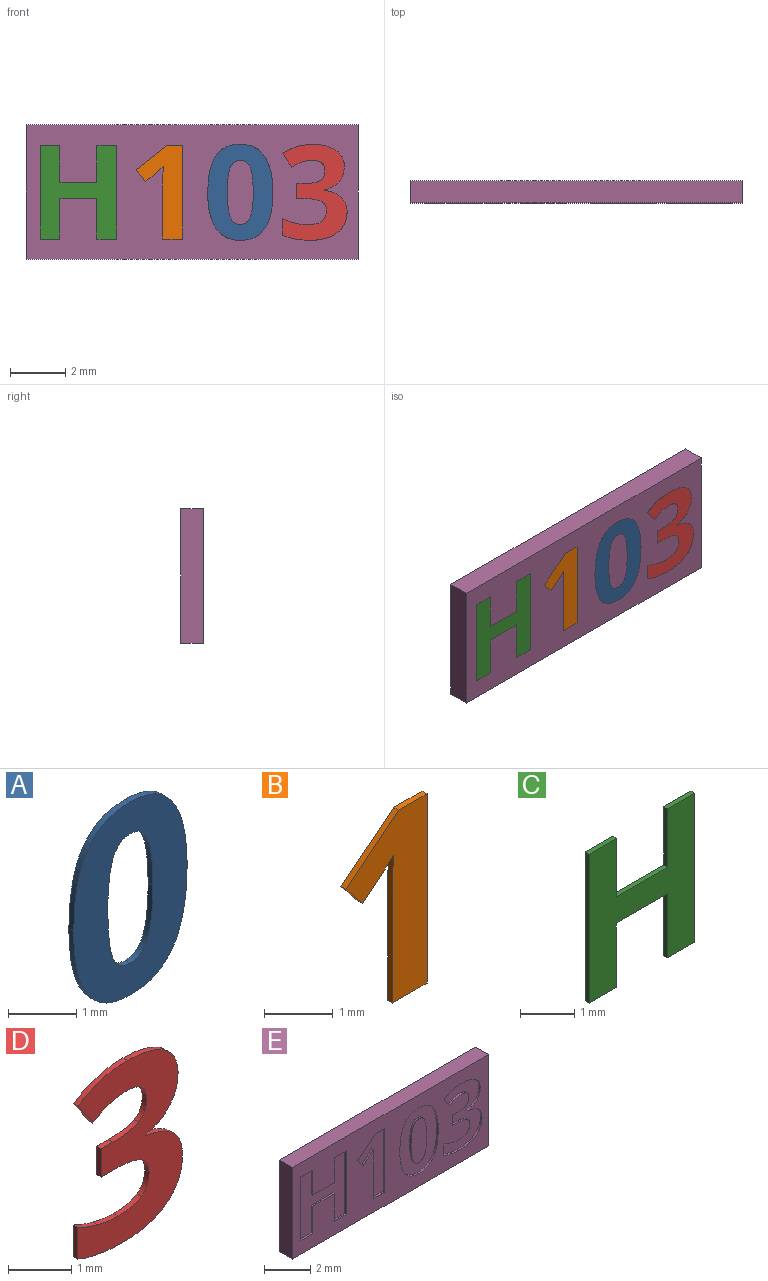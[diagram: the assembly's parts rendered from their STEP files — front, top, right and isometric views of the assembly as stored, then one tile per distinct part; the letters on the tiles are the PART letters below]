
ASSEMBLY  parts=5 mates=4
PART A: 18 faces, bbox 2.4x0.1x3.5 mm
  f0: plane 3.47x2.36mm, normal (0,-1,0), area 5mm2, adj f1,f2,f3,f4,f5,f6,f7,f8
  f1: extruded ~0.88x0.44mm, area 0.1mm2, adj f0,f2,f11,f13
  f2: extruded ~0.89x0.42mm, area 0.1mm2, adj f0,f1,f3,f11
  f3: extruded ~1.32x0.29mm, area 0.1mm2, adj f0,f2,f4,f11
  f4: extruded ~1.29x0.3mm, area 0.1mm2, adj f0,f3,f5,f11
  f5: extruded ~0.88x0.44mm, area 0.1mm2, adj f0,f4,f11,f12
  f6: extruded ~0.36x0.27mm, area 0mm2, adj f0,f7,f11,f16
  f7: extruded ~0.36x0.27mm, area 0mm2, adj f0,f6,f8,f11
  f8: extruded ~0.89x0.11mm, area 0.1mm2, adj f0,f7,f9,f11
  f9: extruded ~0.89x0.11mm, area 0.1mm2, adj f0,f8,f10,f11
  f10: extruded ~0.36x0.27mm, area 0mm2, adj f0,f9,f11,f15
  f11: plane 3.47x2.36mm, normal (0,1,0), area 5mm2, adj f1,f2,f3,f4,f5,f6,f7,f8
  f12: extruded ~0.89x0.42mm, area 0.1mm2, adj f0,f5,f11,f14
  f13: extruded ~1.3x0.3mm, area 0.1mm2, adj f0,f1,f11,f14
  f14: extruded ~1.31x0.29mm, area 0.1mm2, adj f0,f11,f12,f13
  f15: extruded ~0.36x0.27mm, area 0mm2, adj f0,f10,f11,f17
  f16: extruded ~0.89x0.11mm, area 0.1mm2, adj f0,f6,f11,f17
  f17: extruded ~0.89x0.11mm, area 0.1mm2, adj f0,f11,f15,f16
PART B: 12 faces, bbox 1.7x0.1x3.4 mm
  f0: plane 3.37x1.67mm, normal (0,-1,0), area 2.9mm2, adj f1,f2,f3,f4,f5,f6,f7,f9
  f1: plane 0.59x0.1mm, normal (0,0,1), area 0.1mm2, adj f0,f2,f8,f10
  f2: plane 1.09x0.86mm, normal (-0.62,0,0.78), area 0.1mm2, adj f0,f1,f3,f8
  f3: plane 0.43x0.34mm, normal (-0.78,0,-0.63), area 0.1mm2, adj f0,f2,f4,f8
  f4: plane 0.39x0.31mm, normal (0.63,0,-0.78), area 0mm2, adj f0,f3,f5,f8
  f5: extruded ~0.25x0.23mm, area 0mm2, adj f0,f4,f6,f8
  f6: plane 0.35x0.1mm, normal (-1,0,0.03), area 0mm2, adj f0,f5,f7,f8
  f7: plane 0.32x0.1mm, normal (-1,0,0.02), area 0mm2, adj f0,f6,f8,f9
  f8: plane 3.37x1.67mm, normal (0,1,0), area 2.9mm2, adj f1,f2,f3,f4,f5,f6,f7,f9
  f9: plane 1.95x0.1mm, normal (-1,0,0), area 0.2mm2, adj f0,f7,f8,f11
  f10: plane 3.37x0.1mm, normal (1,0,0), area 0.3mm2, adj f0,f1,f8,f11
  f11: plane 0.71x0.1mm, normal (0,0,-1), area 0.1mm2, adj f0,f8,f9,f10
PART C: 14 faces, bbox 2.8x0.1x3.4 mm
  f0: plane 3.37x2.76mm, normal (0,-1,0), area 5.6mm2, adj f1,f2,f3,f4,f5,f6,f7,f8
  f1: plane 0.71x0.1mm, normal (0,0,1), area 0.1mm2, adj f0,f2,f10,f12
  f2: plane 1.32x0.1mm, normal (-1,0,0), area 0.1mm2, adj f0,f1,f3,f10
  f3: plane 1.33x0.1mm, normal (0,0,1), area 0.1mm2, adj f0,f2,f4,f10
  f4: plane 1.32x0.1mm, normal (1,0,0), area 0.1mm2, adj f0,f3,f5,f10
  f5: plane 0.72x0.1mm, normal (0,0,1), area 0.1mm2, adj f0,f4,f6,f10
  f6: plane 3.37x0.1mm, normal (-1,0,0), area 0.3mm2, adj f0,f5,f7,f10
  f7: plane 0.72x0.1mm, normal (0,0,-1), area 0.1mm2, adj f0,f6,f8,f10
  f8: plane 1.46x0.1mm, normal (1,0,0), area 0.1mm2, adj f0,f7,f9,f10
  f9: plane 1.33x0.1mm, normal (0,0,-1), area 0.1mm2, adj f0,f8,f10,f11
  f10: plane 3.37x2.76mm, normal (0,1,0), area 5.6mm2, adj f1,f2,f3,f4,f5,f6,f7,f8
  f11: plane 1.46x0.1mm, normal (-1,0,0), area 0.1mm2, adj f0,f9,f10,f13
  f12: plane 3.37x0.1mm, normal (1,0,0), area 0.3mm2, adj f0,f1,f10,f13
  f13: plane 0.71x0.1mm, normal (0,0,-1), area 0.1mm2, adj f0,f10,f11,f12
PART D: 29 faces, bbox 2.3x0.1x3.5 mm
  f0: plane 3.47x2.33mm, normal (0,-1,0), area 4.3mm2, adj f1,f2,f3,f4,f5,f6,f7,f8
  f1: extruded ~0.83x0.21mm, area 0.1mm2, adj f0,f2,f25,f27
  f2: extruded ~1.1x0.33mm, area 0.1mm2, adj f0,f1,f3,f25
  f3: plane 0.49x0.33mm, normal (-0.83,0,-0.56), area 0.1mm2, adj f0,f2,f4,f25
  f4: extruded ~0.38x0.19mm, area 0mm2, adj f0,f3,f5,f25
  f5: extruded ~0.34x0.1mm, area 0mm2, adj f0,f4,f6,f25
  f6: extruded ~0.48x0.38mm, area 0.1mm2, adj f0,f5,f7,f25
  f7: extruded ~0.35x0.18mm, area 0mm2, adj f0,f6,f8,f25
  f8: extruded ~0.57x0.1mm, area 0.1mm2, adj f0,f7,f9,f25
  f9: plane 0.26x0.1mm, normal (0,0,1), area 0mm2, adj f0,f8,f10,f25
  f10: plane 0.55x0.1mm, normal (-1,0,0), area 0.1mm2, adj f0,f9,f11,f25
  f11: plane 0.26x0.1mm, normal (0,0,-1), area 0mm2, adj f0,f10,f12,f25
  f12: extruded ~0.62x0.1mm, area 0.1mm2, adj f0,f11,f13,f25
  f13: extruded ~0.34x0.19mm, area 0mm2, adj f0,f12,f14,f25
  f14: extruded ~0.39x0.17mm, area 0mm2, adj f0,f13,f15,f25
  f15: extruded ~0.52x0.12mm, area 0.1mm2, adj f0,f14,f16,f25
  f16: extruded ~0.47x0.1mm, area 0mm2, adj f0,f15,f17,f25
  f17: extruded ~0.43x0.16mm, area 0mm2, adj f0,f16,f18,f25
  f18: plane 0.61x0.1mm, normal (-1,0,0), area 0.1mm2, adj f0,f17,f19,f25
  f19: extruded ~0.97x0.18mm, area 0.1mm2, adj f0,f18,f20,f25
  f20: extruded ~1.01x0.27mm, area 0.1mm2, adj f0,f19,f21,f25
  f21: extruded ~0.76x0.35mm, area 0.1mm2, adj f0,f20,f22,f25
  f22: extruded ~0.53x0.21mm, area 0.1mm2, adj f0,f21,f23,f25
  f23: extruded ~0.62x0.25mm, area 0.1mm2, adj f0,f22,f24,f25
  f24: plane 0.1x0.01mm, normal (1,0,0), area 0mm2, adj f0,f23,f25,f26
  f25: plane 3.47x2.33mm, normal (0,1,0), area 4.3mm2, adj f1,f2,f3,f4,f5,f6,f7,f8
  f26: extruded ~0.54x0.3mm, area 0.1mm2, adj f0,f24,f25,f28
  f27: extruded ~0.59x0.3mm, area 0.1mm2, adj f0,f1,f25,f28
  f28: extruded ~0.54x0.19mm, area 0.1mm2, adj f0,f25,f26,f27
PART E: 76 faces, bbox 12x0.8x4.9 mm
  f0: plane 12x4.85mm, normal (0,-1,0), area 38.5mm2, adj f1,f2,f3,f4,f6,f7,f8,f9
  f1: plane 4.85x0.8mm, normal (1,0,0), area 3.9mm2, adj f0,f2,f4,f5
  f2: plane 12x0.8mm, normal (0,0,1), area 9.6mm2, adj f0,f1,f3,f5
  f3: plane 4.85x0.8mm, normal (-1,0,0), area 3.9mm2, adj f0,f2,f4,f5
  f4: plane 12x0.8mm, normal (0,0,-1), area 9.6mm2, adj f0,f1,f3,f5
  f5: plane 12x4.85mm, normal (0,1,0), area 58.2mm2, adj f1,f2,f3,f4
  f6: plane 3.37x0.1mm, normal (-1,0,0), area 0.3mm2, adj f0,f7,f15,f16
  f7: plane 0.59x0.1mm, normal (0,0,-1), area 0.1mm2, adj f0,f6,f8,f16
  f8: plane 1.09x0.86mm, normal (0.62,0,-0.78), area 0.1mm2, adj f0,f7,f9,f16
  f9: plane 0.43x0.34mm, normal (0.78,0,0.63), area 0.1mm2, adj f0,f8,f10,f16
  f10: plane 0.39x0.31mm, normal (-0.63,0,0.78), area 0mm2, adj f0,f9,f11,f16
  f11: extruded ~0.25x0.23mm, area 0mm2, adj f0,f10,f12,f16
  f12: plane 0.35x0.1mm, normal (1,0,-0.03), area 0mm2, adj f0,f11,f13,f16
  f13: plane 0.32x0.1mm, normal (1,0,-0.02), area 0mm2, adj f0,f12,f14,f16
  f14: plane 1.95x0.1mm, normal (1,0,0), area 0.2mm2, adj f0,f13,f15,f16
  f15: plane 0.71x0.1mm, normal (0,0,1), area 0.1mm2, adj f0,f6,f14,f16
  f16: plane 3.37x1.67mm, normal (0,-1,0), area 2.9mm2, adj f6,f7,f8,f9,f10,f11,f12,f13
  f17: extruded ~0.59x0.3mm, area 0.1mm2, adj f0,f18,f43,f44
  f18: extruded ~0.83x0.21mm, area 0.1mm2, adj f0,f17,f19,f44
  f19: extruded ~1.1x0.33mm, area 0.1mm2, adj f0,f18,f20,f44
  f20: plane 0.49x0.33mm, normal (0.83,0,0.56), area 0.1mm2, adj f0,f19,f21,f44
  f21: extruded ~0.38x0.19mm, area 0mm2, adj f0,f20,f22,f44
  f22: extruded ~0.34x0.1mm, area 0mm2, adj f0,f21,f23,f44
  f23: extruded ~0.48x0.38mm, area 0.1mm2, adj f0,f22,f24,f44
  f24: extruded ~0.35x0.18mm, area 0mm2, adj f0,f23,f25,f44
  f25: extruded ~0.57x0.1mm, area 0.1mm2, adj f0,f24,f26,f44
  f26: plane 0.26x0.1mm, normal (0,0,-1), area 0mm2, adj f0,f25,f27,f44
  f27: plane 0.55x0.1mm, normal (1,0,0), area 0.1mm2, adj f0,f26,f28,f44
  f28: plane 0.26x0.1mm, normal (0,0,1), area 0mm2, adj f0,f27,f29,f44
  f29: extruded ~0.62x0.1mm, area 0.1mm2, adj f0,f28,f30,f44
  f30: extruded ~0.34x0.19mm, area 0mm2, adj f0,f29,f31,f44
  f31: extruded ~0.39x0.17mm, area 0mm2, adj f0,f30,f32,f44
  f32: extruded ~0.52x0.12mm, area 0.1mm2, adj f0,f31,f33,f44
  f33: extruded ~0.47x0.1mm, area 0mm2, adj f0,f32,f34,f44
  f34: extruded ~0.43x0.16mm, area 0mm2, adj f0,f33,f35,f44
  f35: plane 0.61x0.1mm, normal (1,0,0), area 0.1mm2, adj f0,f34,f36,f44
  f36: extruded ~0.97x0.18mm, area 0.1mm2, adj f0,f35,f37,f44
  f37: extruded ~1.01x0.27mm, area 0.1mm2, adj f0,f36,f38,f44
  f38: extruded ~0.76x0.35mm, area 0.1mm2, adj f0,f37,f39,f44
  f39: extruded ~0.53x0.21mm, area 0.1mm2, adj f0,f38,f40,f44
  f40: extruded ~0.62x0.25mm, area 0.1mm2, adj f0,f39,f41,f44
  f41: plane 0.1x0.01mm, normal (-1,0,0), area 0mm2, adj f0,f40,f42,f44
  f42: extruded ~0.54x0.3mm, area 0.1mm2, adj f0,f41,f43,f44
  f43: extruded ~0.54x0.19mm, area 0.1mm2, adj f0,f17,f42,f44
  f44: plane 3.47x2.33mm, normal (0,-1,0), area 4.3mm2, adj f17,f18,f19,f20,f21,f22,f23,f24
  f45: extruded ~1.3x0.3mm, area 0.1mm2, adj f0,f46,f60,f61
  f46: extruded ~0.88x0.44mm, area 0.1mm2, adj f0,f45,f47,f61
  f47: extruded ~0.89x0.42mm, area 0.1mm2, adj f0,f46,f48,f61
  f48: extruded ~1.32x0.29mm, area 0.1mm2, adj f0,f47,f49,f61
  f49: extruded ~1.29x0.3mm, area 0.1mm2, adj f0,f48,f50,f61
  f50: extruded ~0.88x0.44mm, area 0.1mm2, adj f0,f49,f51,f61
  f51: extruded ~0.89x0.42mm, area 0.1mm2, adj f0,f50,f60,f61
  f52: extruded ~0.89x0.11mm, area 0.1mm2, adj f53,f59,f61,f62
  f53: extruded ~0.36x0.27mm, area 0mm2, adj f52,f54,f61,f62
  f54: extruded ~0.36x0.27mm, area 0mm2, adj f53,f55,f61,f62
  f55: extruded ~0.89x0.11mm, area 0.1mm2, adj f54,f56,f61,f62
  f56: extruded ~0.89x0.11mm, area 0.1mm2, adj f55,f57,f61,f62
  f57: extruded ~0.36x0.27mm, area 0mm2, adj f56,f58,f61,f62
  f58: extruded ~0.36x0.27mm, area 0mm2, adj f57,f59,f61,f62
  f59: extruded ~0.89x0.11mm, area 0.1mm2, adj f52,f58,f61,f62
  f60: extruded ~1.31x0.29mm, area 0.1mm2, adj f0,f45,f51,f61
  f61: plane 3.47x2.36mm, normal (0,-1,0), area 5mm2, adj f45,f46,f47,f48,f49,f50,f51,f52
  f62: plane 2.32x0.94mm, normal (0,-1,0), area 1.8mm2, adj f52,f53,f54,f55,f56,f57,f58,f59
  f63: plane 3.37x0.1mm, normal (-1,0,0), area 0.3mm2, adj f0,f64,f74,f75
  f64: plane 0.71x0.1mm, normal (0,0,-1), area 0.1mm2, adj f0,f63,f65,f75
  f65: plane 1.32x0.1mm, normal (1,0,0), area 0.1mm2, adj f0,f64,f66,f75
  f66: plane 1.33x0.1mm, normal (0,0,-1), area 0.1mm2, adj f0,f65,f67,f75
  f67: plane 1.32x0.1mm, normal (-1,0,0), area 0.1mm2, adj f0,f66,f68,f75
  f68: plane 0.72x0.1mm, normal (0,0,-1), area 0.1mm2, adj f0,f67,f69,f75
  f69: plane 3.37x0.1mm, normal (1,0,0), area 0.3mm2, adj f0,f68,f70,f75
  f70: plane 0.72x0.1mm, normal (0,0,1), area 0.1mm2, adj f0,f69,f71,f75
  f71: plane 1.46x0.1mm, normal (-1,0,0), area 0.1mm2, adj f0,f70,f72,f75
  f72: plane 1.33x0.1mm, normal (0,0,1), area 0.1mm2, adj f0,f71,f73,f75
  f73: plane 1.46x0.1mm, normal (1,0,0), area 0.1mm2, adj f0,f72,f74,f75
  f74: plane 0.71x0.1mm, normal (0,0,1), area 0.1mm2, adj f0,f63,f73,f75
  f75: plane 3.37x2.76mm, normal (0,-1,0), area 5.6mm2, adj f63,f64,f65,f66,f67,f68,f69,f70
PLACE A t=(-1.16,0.29,-0.11)mm
PLACE B t=(-2.79,0.29,-0.11)mm
PLACE C t=(-0.06,0.29,-0.11)mm
PLACE D t=(2.88,0.29,-0.11)mm
PLACE E t=(-0.06,0.29,-0.11)mm
MATE fastened C.f0 <-> E.f0  axis (0,-1,0) through (-5.54,-0.51,-1.81)mm
MATE fastened B.f0 <-> E.f0  axis (0,-1,0) through (-1.12,-0.51,-1.81)mm
MATE fastened D.f0 <-> E.f0  axis (0,-1,0) through (3.22,-0.51,-1.68)mm
MATE fastened A.f0 <-> E.f62  axis (0,-1,0) through (1.69,-0.51,-1.29)mm
